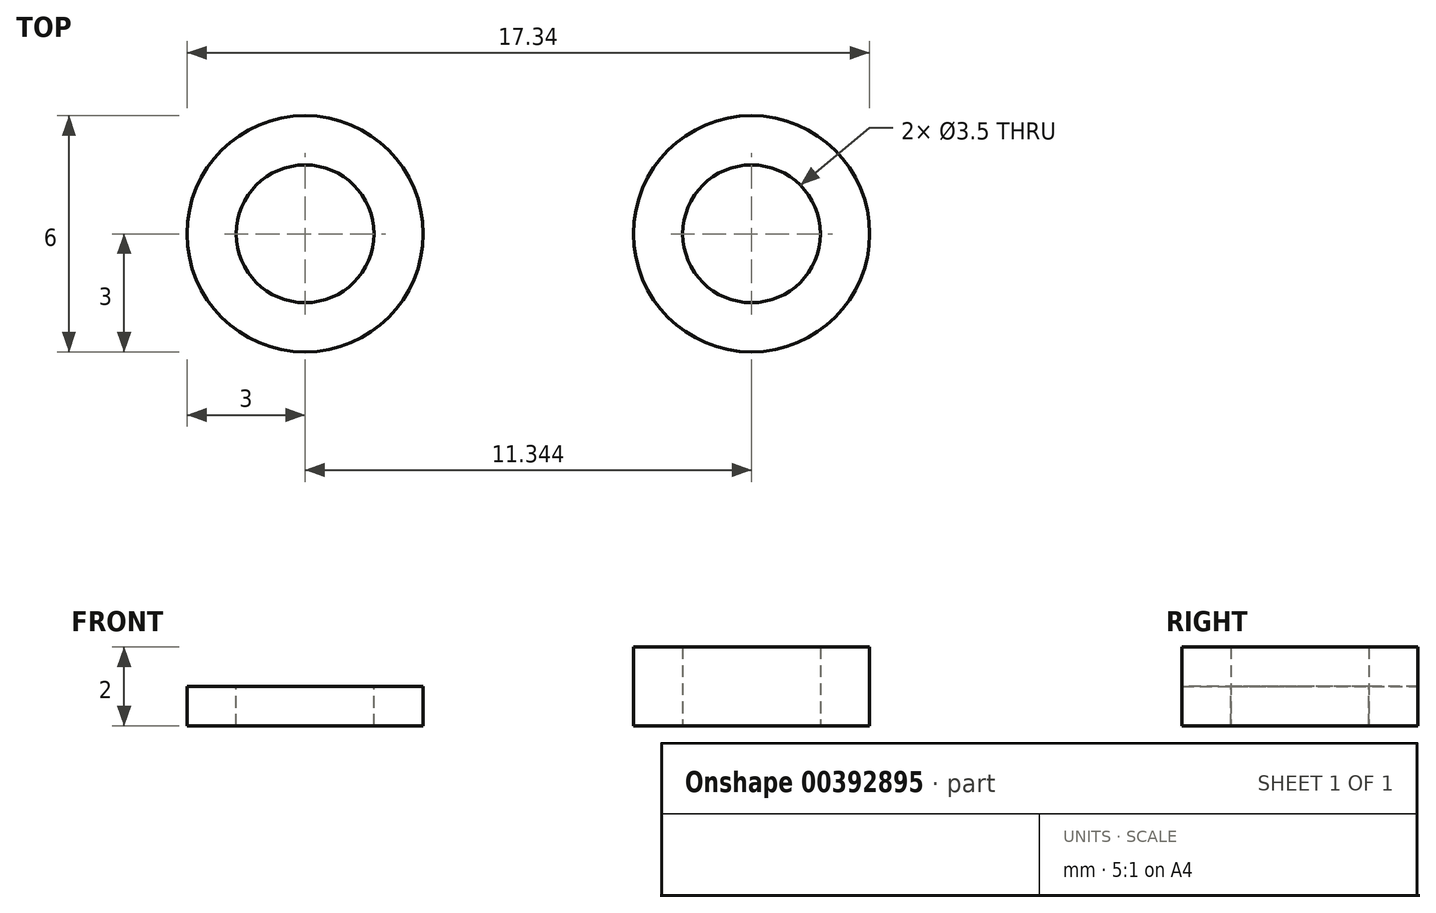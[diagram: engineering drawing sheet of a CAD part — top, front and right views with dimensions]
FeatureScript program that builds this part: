
annotation { "Feature Type Name" : "Feature", "Feature Type Description" : "" }
export const myFeature = defineFeature(function(context is Context, id is Id, definition is map)
    precondition{}
    {
        {
            var Q0;
            Q0=qCreatedBy(makeId("Top.planeOp"),FACE);
            var sketch = newSketch(context, id + "F0", { "sketchPlane" : qUnion([Q0])});
            skCircle(sketch, "E0", {"center": v(0, 0) * mm, "radius": 3 * mm});
            skSolve(sketch);
        }
        {
            var Q0;
            Q0 = qSketchRegion(id + "F0", true);
            extrude(context, id + "F1", {"entities" : qUnion([Q0]), "depth" : 1 * mm});
        }
        {
            var Q0;
            Q0=makeQuery(id+"F1.opExtrude","CAP_FACE",FACE,{"disambiguationData":[OSD([sQuery(id+"F0.wireOp",EDGE,"E0")])],"isStart":false});
            var sketch = newSketch(context, id + "F2", { "sketchPlane" : qUnion([Q0])});
            skCircle(sketch, "E1", {"center": v(0, 0) * mm, "radius": 1.75 * mm});
            skSolve(sketch);
        }
        {
            var Q0;
            Q0=makeQuery(id+"F2.imprint","IMPRINT",FACE,{"disambiguationData":[TD([[makeQuery(id+"F2.imprint","IMPRINT",EDGE,{"derivedFrom":sQuery(id+"F2.wireOp",EDGE,"E1")}),1.0]])]});
            extrude(context, id + "F3", {"entities" : qUnion([Q0]), "operationType" : NewBodyOperationType.REMOVE, "oppositeDirection" : true, "depth" : 25 * mm});
        }
        {
            var Q0;
            Q0=qCreatedBy(makeId("Top.planeOp"),FACE);
            var sketch = newSketch(context, id + "F4", { "sketchPlane" : qUnion([Q0])});
            skCircle(sketch, "E2", {"center": v(11.34, 0) * mm, "radius": 3 * mm});
            skCircle(sketch, "E3", {"center": v(11.34, 0) * mm, "radius": 1.75 * mm});
            skSolve(sketch);
        }
        {
            var Q0;
            Q0 = qSketchRegion(id + "F4", true);
            extrude(context, id + "F5", {"entities" : qUnion([Q0]), "depth" : 2 * mm});
        }
    });
